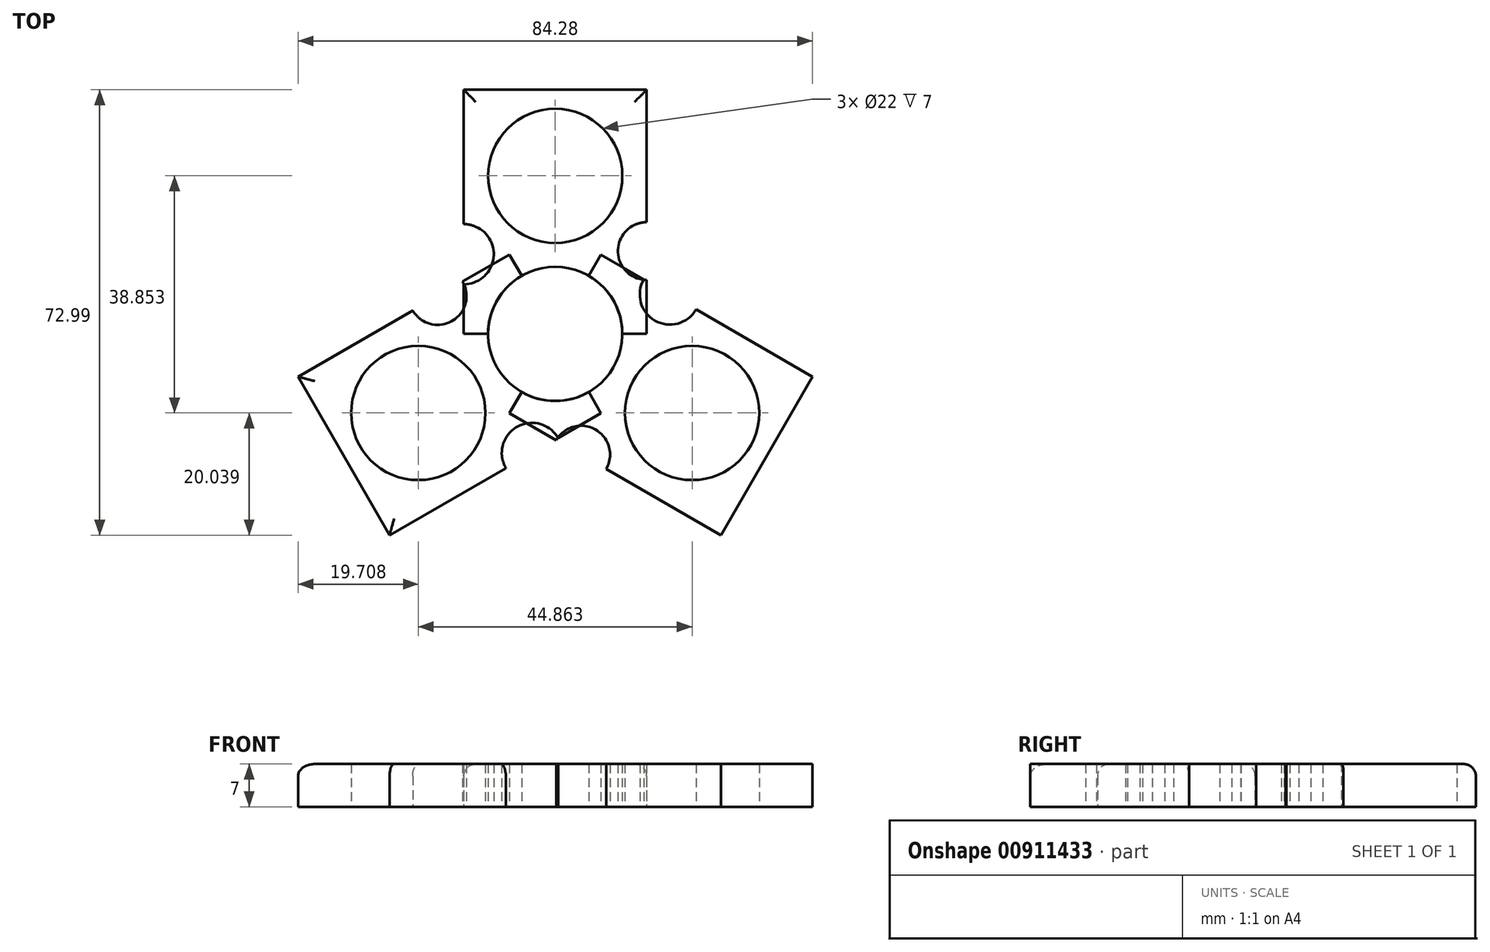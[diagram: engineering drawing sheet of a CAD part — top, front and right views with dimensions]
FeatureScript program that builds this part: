
annotation { "Feature Type Name" : "Feature", "Feature Type Description" : "" }
export const myFeature = defineFeature(function(context is Context, id is Id, definition is map)
    precondition{}
    {
        {
            var Q0;
            Q0=qCreatedBy(makeId("Top.planeOp"),FACE);
            var sketch = newSketch(context, id + "F0", { "sketchPlane" : qUnion([Q0])});
            skCircle(sketch, "E0", {"center": v(0, 0) * mm, "radius": 11 * mm});
            skLineSegment(sketch, "E1.bottom", {"start": v(0, 0) * mm, "end": v(15, 0) * mm});
            skLineSegment(sketch, "E1.top", {"start": v(0, 40) * mm, "end": v(15, 40) * mm});
            skLineSegment(sketch, "E1.left", {"start": v(0, 0) * mm, "end": v(0, 40) * mm});
            skLineSegment(sketch, "E1.right", {"start": v(15, 0) * mm, "end": v(15, 40) * mm});
            skLineSegment(sketch, "E2.bottom", {"start": v(0, 0) * mm, "end": v(-15, 0) * mm});
            skLineSegment(sketch, "E2.top", {"start": v(0, 40) * mm, "end": v(-15, 40) * mm});
            skLineSegment(sketch, "E2.right", {"start": v(-15, 0) * mm, "end": v(-15, 40) * mm});
            skLineSegment(sketch, "E3", {"start": v(0, 40) * mm, "end": v(0, 25.9) * mm});
            skCircle(sketch, "E4", {"center": v(0, 25.9) * mm, "radius": 11 * mm});
            skCircle(sketch, "E5", {"center": v(-15, 13.05) * mm, "radius": 4.94 * mm});
            skCircle(sketch, "E6", {"center": v(15, 13.58) * mm, "radius": 4.73 * mm});
            skSolve(sketch);
        }
        {
            var Q0;
            {var subQ0=sQuery(id+"F0.wireOp",EDGE,"E2.top");Q0=makeQuery(id+"F0.imprint","IMPRINT",FACE,{"disambiguationData":[TD([[makeQuery(id+"F0.imprint","IMPRINT",EDGE,{"derivedFrom":subQ0}),1.0]])]});}
            var Q1;
            {var subQ9=sQuery(id+"F0.wireOp",EDGE,"E1.top");Q1=makeQuery(id+"F0.imprint","IMPRINT",FACE,{"disambiguationData":[TD([[makeQuery(id+"F0.imprint","IMPRINT",EDGE,{"derivedFrom":subQ9}),-1.0]])]});}
            extrude(context, id + "F1", {"entities" : qUnion([Q0, Q1]), "depth" : 7 * mm, "offsetDistance" : 25 * mm});
        }
        {
            var Q0;
            Q0=qCreatedBy(makeId("Front.planeOp"),FACE);
            var sketch = newSketch(context, id + "F2", { "sketchPlane" : qUnion([Q0])});
            skLineSegment(sketch, "E7", {"start": v(0, 0) * mm, "end": v(0, 65.3) * mm});
            skSolve(sketch);
        }
        {
            var Q0;
            Q0=makeQuery(id+"F1.opExtrude","SWEPT_BODY",BODY,{"disambiguationData":[OSD([sQuery(id+"F0.wireOp",EDGE,"E0"),sQuery(id+"F0.wireOp",EDGE,"E1.bottom"),sQuery(id+"F0.wireOp",EDGE,"E1.top"),sQuery(id+"F0.wireOp",EDGE,"E1.right"),sQuery(id+"F0.wireOp",EDGE,"E2.bottom"),sQuery(id+"F0.wireOp",EDGE,"E2.top"),sQuery(id+"F0.wireOp",EDGE,"E2.right"),sQuery(id+"F0.wireOp",EDGE,"E4")])]});
            var Q1;
            Q1=sQuery(id+"F2.wireOp",EDGE,"E7");
            transform(context, id + "F3", {"entities" : qUnion([Q0]), "transformType" : TransformType.ROTATION, "transformAxis" : qUnion([Q1]), "angle" : 120 * degree, "makeCopy" : true});
        }
        {
            var Q0;
            Q0=makeQuery(id+"F1.opExtrude","SWEPT_BODY",BODY,{"disambiguationData":[OSD([sQuery(id+"F0.wireOp",EDGE,"E0"),sQuery(id+"F0.wireOp",EDGE,"E1.bottom"),sQuery(id+"F0.wireOp",EDGE,"E1.top"),sQuery(id+"F0.wireOp",EDGE,"E1.right"),sQuery(id+"F0.wireOp",EDGE,"E2.bottom"),sQuery(id+"F0.wireOp",EDGE,"E2.top"),sQuery(id+"F0.wireOp",EDGE,"E2.right"),sQuery(id+"F0.wireOp",EDGE,"E4")])]});
            var Q1;
            Q1=sQuery(id+"F2.wireOp",EDGE,"E7");
            transform(context, id + "F4", {"entities" : qUnion([Q0]), "transformType" : TransformType.ROTATION, "transformAxis" : qUnion([Q1]), "angle" : 240 * degree, "makeCopy" : true});
        }
        {
            var Q0;
            {var subQ0=sQuery(id+"F0.wireOp",EDGE,"E1.right");Q0=makeQuery(id+"F1.opExtrude","CAP_EDGE",EDGE,{"disambiguationData":[OSD([subQ0]),TDD([makeQuery(id+"F0.imprint","IMPRINT",EDGE,{"disambiguationData":[TD([[makeQuery(id+"F0.imprint","INTERSECT",VERTEX,{"derivedFrom":[sQuery(id+"F0.wireOp",EDGE,"E1.top"),subQ0]}),1.0]])],"derivedFrom":subQ0})])],"isStart":false});}
            var Q1;
            Q1=makeQuery(id+"F1.opExtrude","CAP_EDGE",EDGE,{"disambiguationData":[OSD([sQuery(id+"F0.wireOp",EDGE,"E1.top"),sQuery(id+"F0.wireOp",EDGE,"E2.top")])],"isStart":false});
            var Q2;
            {var subQ0=sQuery(id+"F0.wireOp",EDGE,"E2.right");Q2=makeQuery(id+"F1.opExtrude","CAP_EDGE",EDGE,{"disambiguationData":[OSD([subQ0]),TDD([makeQuery(id+"F0.imprint","IMPRINT",EDGE,{"disambiguationData":[TD([[makeQuery(id+"F0.imprint","INTERSECT",VERTEX,{"derivedFrom":[sQuery(id+"F0.wireOp",EDGE,"E2.top"),subQ0]}),1.0]])],"derivedFrom":subQ0})])],"isStart":false});}
            var Q3;
            {var subQ0=sQuery(id+"F0.wireOp",EDGE,"E1.right");Q3=makeQuery(id+"F3.opPattern","COPY",EDGE,{"derivedFrom":makeQuery(id+"F1.opExtrude","CAP_EDGE",EDGE,{"disambiguationData":[OSD([subQ0]),TDD([makeQuery(id+"F0.imprint","IMPRINT",EDGE,{"disambiguationData":[TD([[makeQuery(id+"F0.imprint","INTERSECT",VERTEX,{"derivedFrom":[sQuery(id+"F0.wireOp",EDGE,"E1.top"),subQ0]}),1.0]])],"derivedFrom":subQ0})])],"isStart":false}),"instanceName":"1"});}
            var Q4;
            {var subQ0=sQuery(id+"F0.wireOp",EDGE,"E2.right");Q4=makeQuery(id+"F3.opPattern","COPY",EDGE,{"derivedFrom":makeQuery(id+"F1.opExtrude","CAP_EDGE",EDGE,{"disambiguationData":[OSD([subQ0]),TDD([makeQuery(id+"F0.imprint","IMPRINT",EDGE,{"disambiguationData":[TD([[makeQuery(id+"F0.imprint","INTERSECT",VERTEX,{"derivedFrom":[sQuery(id+"F0.wireOp",EDGE,"E2.top"),subQ0]}),1.0]])],"derivedFrom":subQ0})])],"isStart":false}),"instanceName":"1"});}
            var Q5;
            Q5=makeQuery(id+"F3.opPattern","COPY",EDGE,{"derivedFrom":makeQuery(id+"F1.opExtrude","CAP_EDGE",EDGE,{"disambiguationData":[OSD([sQuery(id+"F0.wireOp",EDGE,"E1.top"),sQuery(id+"F0.wireOp",EDGE,"E2.top")])],"isStart":false}),"instanceName":"1"});
            fillet(context, id + "F5", {"entities" : qUnion([Q0, Q1, Q2, Q3, Q4, Q5]), "radius" : 2 * mm, "tangentPropagation" : true, "allowEdgeOverflow" : false});
        }
    });
